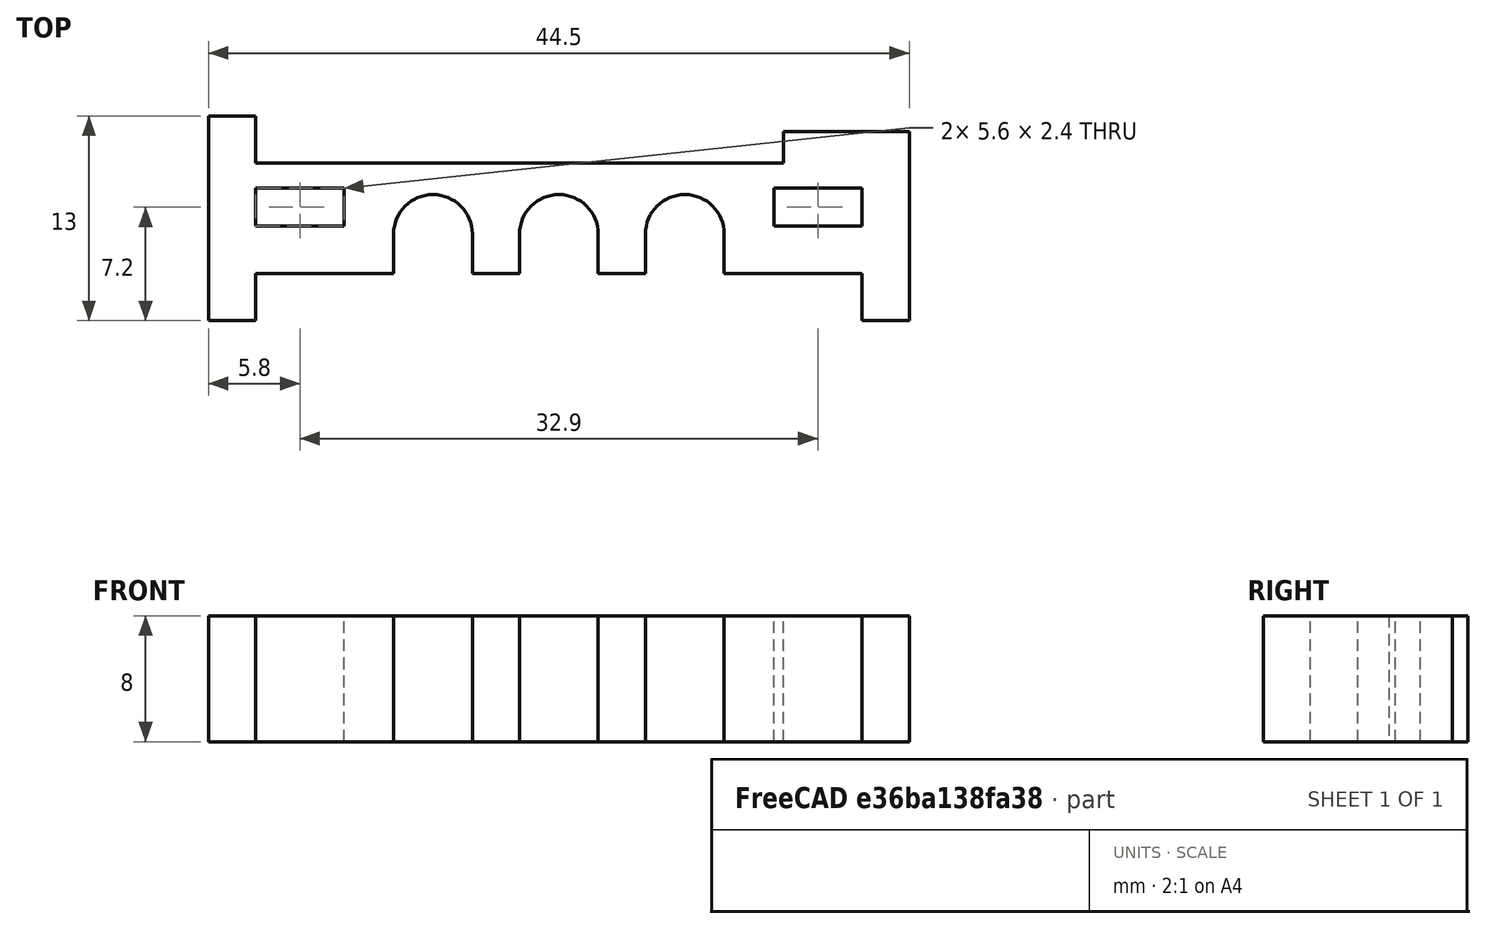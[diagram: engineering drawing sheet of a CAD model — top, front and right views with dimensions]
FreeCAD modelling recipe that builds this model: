
FCSTD DOCUMENT  (FreeCAD 0.19R24291 (Git))
Label: ri_parm-soundsupport
License: All rights reserved
LicenseURL: http://en.wikipedia.org/wiki/All_rights_reserved
objects: Sketcher::SketchObject×1, PartDesign::Pad×1, PartDesign::Body×1
note: 4 computed .brp shape members not serialized (recipe doc carries the construction recipe); baked Part::Feature solids carry a one-line shape summary decoded from their .brp

FEATURE [Sketcher::SketchObject] Sketch
  FullyConstrained = true
  MapMode = 5
  Support = -> [XY_Plane]
  expr: Constraints[71] = .Constraints.radius
  sketch-geometry (32):
    g0: LineSegment StartX=-22.25 StartY=-3 StartZ=0 EndX=-19.25 EndY=-3 EndZ=0
    g1: LineSegment StartX=-19.25 StartY=-3 StartZ=0 EndX=-19.25 EndY=9e-16 EndZ=0
    g2: LineSegment StartX=-19.25 StartY=7e-16 StartZ=0 EndX=-10.5 EndY=7e-16 EndZ=0
    g3: LineSegment StartX=-10.5 StartY=7e-16 StartZ=0 EndX=-10.5 EndY=2.5 EndZ=0
    g4: LineSegment StartX=-5.5 StartY=2.5 StartZ=0 EndX=-5.5 EndY=9e-16 EndZ=0
    g5: LineSegment StartX=-5.5 StartY=7e-16 StartZ=0 EndX=-2.5 EndY=7e-16 EndZ=0
    g6: LineSegment StartX=-2.5 StartY=7e-16 StartZ=0 EndX=-2.5 EndY=2.5 EndZ=0
    g7: LineSegment StartX=2.5 StartY=2.5 StartZ=0 EndX=2.5 EndY=-9e-16 EndZ=0
    g8: LineSegment StartX=2.5 StartY=-9e-16 StartZ=0 EndX=5.5 EndY=-9e-16 EndZ=0
    g9: LineSegment StartX=5.5 StartY=-9e-16 StartZ=0 EndX=5.5 EndY=2.5 EndZ=0
    g10: LineSegment StartX=10.5 StartY=2.5 StartZ=0 EndX=10.5 EndY=-9e-16 EndZ=0
    g11: LineSegment StartX=10.5 StartY=-9e-16 StartZ=0 EndX=19.25 EndY=-9e-16 EndZ=0
    g12: LineSegment StartX=19.25 StartY=-9e-16 StartZ=0 EndX=19.25 EndY=-3 EndZ=0
    g13: LineSegment StartX=19.25 StartY=-3 StartZ=0 EndX=22.25 EndY=-3 EndZ=0
    g14: LineSegment StartX=22.25 StartY=-3 StartZ=0 EndX=22.25 EndY=9 EndZ=0
    g15: LineSegment StartX=22.25 StartY=9 StartZ=0 EndX=14.25 EndY=9 EndZ=0
    g16: LineSegment StartX=14.25 StartY=9 StartZ=0 EndX=14.25 EndY=7 EndZ=0
    g17: LineSegment StartX=14.25 StartY=7 StartZ=0 EndX=-19.25 EndY=7 EndZ=0
    g18: LineSegment StartX=-19.25 StartY=7 StartZ=0 EndX=-19.25 EndY=10 EndZ=0
    g19: LineSegment StartX=-19.25 StartY=10 StartZ=0 EndX=-22.25 EndY=10 EndZ=0
    g20: LineSegment StartX=-22.25 StartY=10 StartZ=0 EndX=-22.25 EndY=-3 EndZ=0
    g21: ArcOfCircle CenterX=-8 CenterY=2.5 CenterZ=0 NormalX=0 NormalY=0 NormalZ=1 AngleXU=0 Radius=2.5 StartAngle=9.24543e-09 EndAngle=3.14159
    g22: ArcOfCircle CenterX=-6e-16 CenterY=2.5 CenterZ=0 NormalX=0 NormalY=0 NormalZ=1 AngleXU=0 Radius=2.5 StartAngle=8.15721e-09 EndAngle=3.14159
    g23: ArcOfCircle CenterX=8 CenterY=2.5 CenterZ=0 NormalX=0 NormalY=0 NormalZ=1 AngleXU=0 Radius=2.5 StartAngle=1.41848e-08 EndAngle=3.14159
    g24: LineSegment StartX=-19.25 StartY=5.4 StartZ=0 EndX=-13.65 EndY=5.4 EndZ=0
    g25: LineSegment StartX=-13.65 StartY=5.4 StartZ=0 EndX=-13.65 EndY=3 EndZ=0
    g26: LineSegment StartX=-13.65 StartY=3 StartZ=0 EndX=-19.25 EndY=3 EndZ=0
    g27: LineSegment StartX=-19.25 StartY=3 StartZ=0 EndX=-19.25 EndY=5.4 EndZ=0
    g28: LineSegment StartX=13.65 StartY=5.4 StartZ=0 EndX=19.25 EndY=5.4 EndZ=0
    g29: LineSegment StartX=19.25 StartY=5.4 StartZ=0 EndX=19.25 EndY=3 EndZ=0
    g30: LineSegment StartX=19.25 StartY=3 StartZ=0 EndX=13.65 EndY=3 EndZ=0
    g31: LineSegment StartX=13.65 StartY=3 StartZ=0 EndX=13.65 EndY=5.4 EndZ=0
  constraints (98):
    c: Horizontal(g0)
    c: Coincident(g0,g1)
    c: Vertical(g1)
    c: Coincident(g1,g2)
    c: Horizontal(g2)
    c: Coincident(g2,g3)
    c: Vertical(g3)
    c: Vertical(g4)
    c: Coincident(g4,g5)
    c: Horizontal(g5)
    c: Coincident(g5,g6)
    c: Vertical(g6)
    c: Vertical(g7)
    c: Coincident(g7,g8)
    c: Horizontal(g8)
    c: Coincident(g8,g9)
    c: Vertical(g9)
    c: Vertical(g10)
    c: Coincident(g10,g11)
    c: Horizontal(g11)
    c: Coincident(g11,g12)
    c: Vertical(g12)
    c: Coincident(g12,g13)
    c: Horizontal(g13)
    c: Coincident(g13,g14)
    c: Vertical(g14)
    c: Coincident(g14,g15)
    c: Horizontal(g15)
    c: Coincident(g15,g16)
    c: Coincident(g16,g17)
    c: Horizontal(g17)
    c: Coincident(g17,g18)
    c: Vertical(g18)
    c: Coincident(g18,g19)
    c: Horizontal(g19)
    c: Coincident(g19,g20)
    c: Coincident(g20,g0)
    c: Vertical(g20)
    c: Vertical(g16)
    c: Equal(g0,g1)
    c: Equal(g1,g12)
    c: Equal(g12,g13)
    c: DistanceX(g0,g0) = 3
    c: Equal(g3,g4)
    c: Equal(g4,g6)
    c: Equal(g6,g7)
    c: Equal(g7,g9)
    c: Equal(g9,g10)
    c: DistanceY(g3,g3) = 2.5  'radius'
    c: DistanceX(g17,g17) = 33.5
    c: DistanceX(g15,g15) = 8
    c: DistanceY(g16,g16) = 2
    c: DistanceY(g18,g18) = 3
    c: DistanceY(g11,g14) = 9
    c: Horizontal(g0,g12)
    c: Horizontal(g4,g2)
    c: Horizontal(g7,g10)
    c: Equal(g18,g19)
    c: Equal(g5,g8)
    c: DistanceX(g5,g5) = 3
    c: Coincident(g21,g4)
    c: Coincident(g21,g3)
    c: Coincident(g22,g7)
    c: Coincident(g22,g6)
    c: Coincident(g23,g10)
    c: Coincident(g23,g9)
    c: Tangent(g21,g3)
    c: Tangent(g22,g6)
    c: Tangent(g23,g9)
    c: Equal(g21,g22)
    c: Equal(g22,g23)
    c: Radius(g21) = 2.5
    c: Equal(g2,g11)
    c: Symmetric(g11,g1,g-1)
    c: Coincident(g24,g25)
    c: Coincident(g25,g26)
    c: Coincident(g26,g27)
    c: Coincident(g27,g24)
    c: Horizontal(g24)
    c: Horizontal(g26)
    c: Vertical(g25)
    c: Vertical(g27)
    c: Coincident(g28,g29)
    c: Coincident(g29,g30)
    c: Coincident(g30,g31)
    c: Coincident(g31,g28)
    c: Horizontal(g28)
    c: Horizontal(g30)
    c: Vertical(g29)
    c: Vertical(g31)
    c: Equal(g27,g31)
    c: Equal(g24,g28)
    c: DistanceY(g27,g27) = 2.4
    c: DistanceX(g24,g24) = 5.6
    c: Vertical(g1,g26)
    c: Vertical(g11,g29)
    c: DistanceY(g1,g26) = 3
    c: Horizontal(g30,g25)
FEATURE [PartDesign::Pad] Pad
  Direction = (1,1,1)
  Length = 8
  Length2 = 100
  Profile = -> Sketch
  Refine = true
  Type = 0
FEATURE [PartDesign::Body] Body
  Group = -> [Sketch,Pad]
  Origin = -> Origin
  Tip = -> Pad
